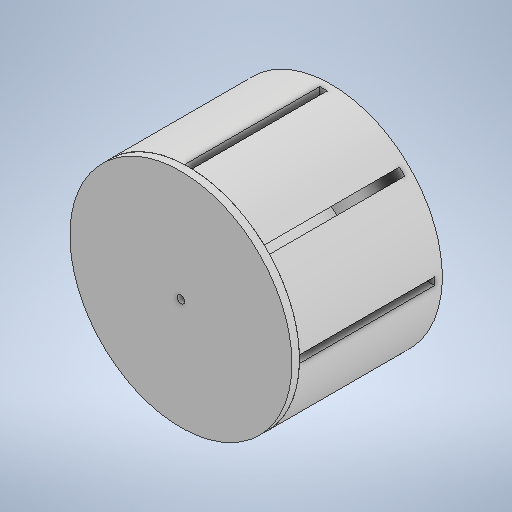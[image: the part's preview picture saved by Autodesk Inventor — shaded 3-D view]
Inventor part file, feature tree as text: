
AUTODESK INVENTOR PART (.ipt)
format: ipt  version: 2025.1 (Build 291241020, 241B)  size: 311,296 bytes
history: native  units: in
note: dims shown in document units (in); Inventor stores cm internally (conversion verified against a paired STEP export)
features: sketch x5, extrude x4
ambient origin geometry x8: Origin, YZ Plane, XZ Plane, XY Plane, X Axis, Y Axis, Z Axis, Center Point
bodies: Solid1 (feature_tree)
feature tree (9):
  sketch  "Sketch1"  dims[d0=5.8268in d1=0.7874in]
  extrude  "Extrusion1"  Depth=0.7874in
  extrude  "Extrusion2"  Depth=0.1969in
  extrude  "Extrusion3"  Depth=0.1969in
  extrude  "Extrusion4"  Depth=0.1969in
  sketch  "Sketch2"  dims[d3=0.1969in d4=2.5761in]
  sketch  "Sketch3"  dims[d5=0.1969in d6=0.1969in]
  sketch  "Sketch4"  dims[d7=2.6183in d8=0.1969in]
  sketch  "Sketch5"  dims[d9=0.1969in d10=0.1969in d11=0.1969in d12=0.1969in d13=3.5433in d14=0.0in d15=0.1969in d16=0.0in d17=0.1969in d18=0.0in d19=0.1969in d20=0.0in d21=0.0in]
